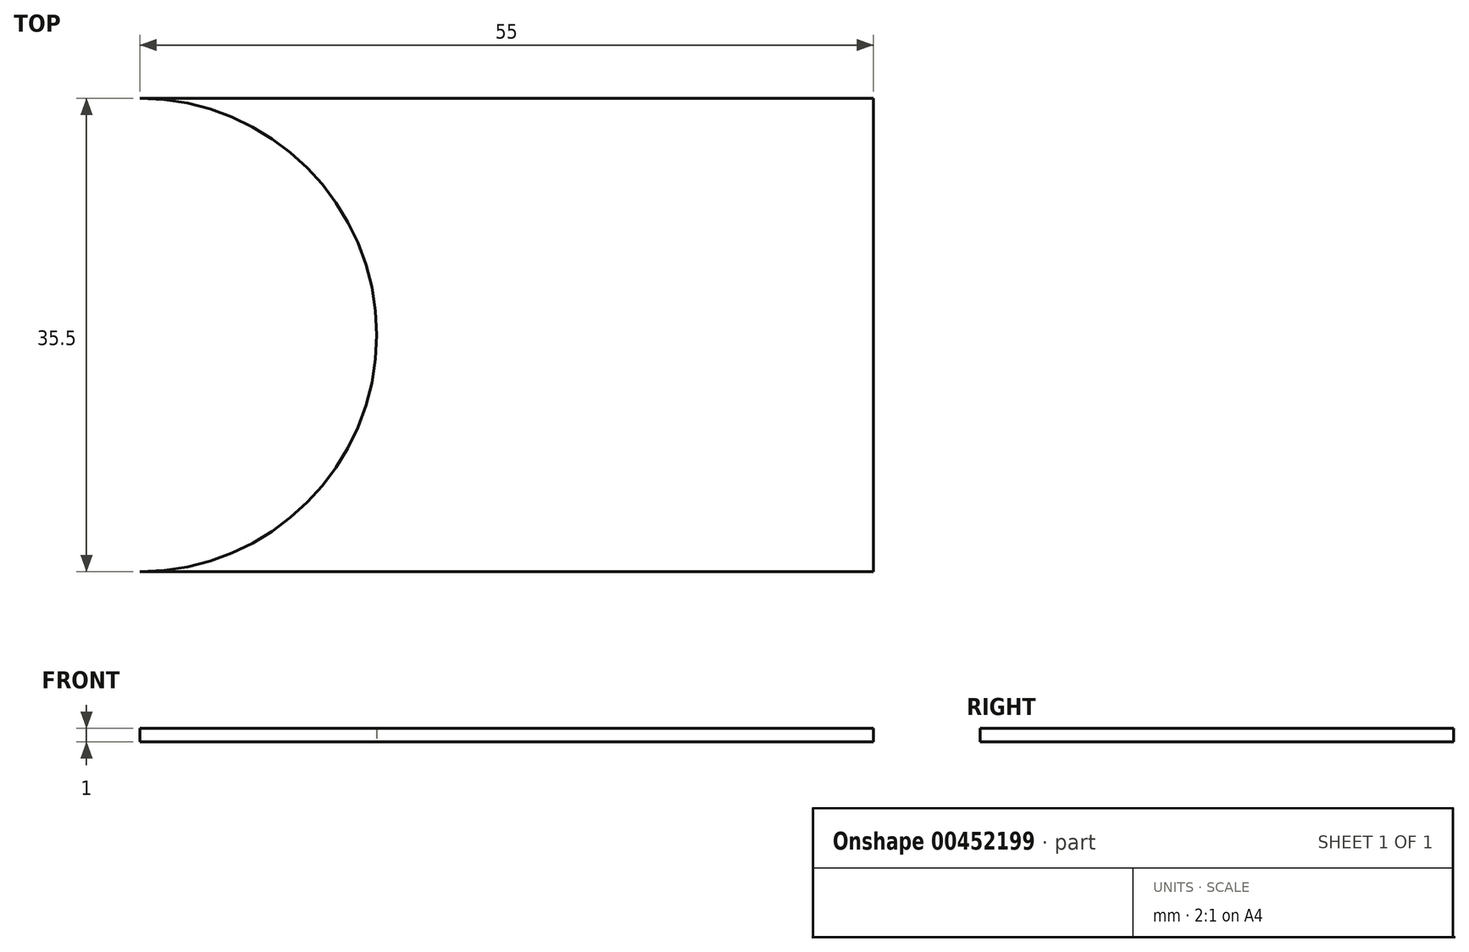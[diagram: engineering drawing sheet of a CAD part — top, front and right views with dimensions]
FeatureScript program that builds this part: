
annotation { "Feature Type Name" : "Feature", "Feature Type Description" : "" }
export const myFeature = defineFeature(function(context is Context, id is Id, definition is map)
    precondition{}
    {
        {
            var Q0;
            Q0=qCreatedBy(makeId("Top.planeOp"),FACE);
            var sketch = newSketch(context, id + "F0", { "sketchPlane" : qUnion([Q0])});
            skCircle(sketch, "E0", {"center": v(0, 0) * mm, "radius": 17.75 * mm});
            skLineSegment(sketch, "E1", {"start": v(0, -17.75) * mm, "end": v(55, -17.75) * mm});
            skLineSegment(sketch, "E2", {"start": v(0, 17.75) * mm, "end": v(55, 17.75) * mm});
            skLineSegment(sketch, "E3", {"start": v(55, 17.75) * mm, "end": v(55, -17.75) * mm});
            skSolve(sketch);
        }
        {
            var Q0;
            {var subQ0=sQuery(id+"F0.wireOp",EDGE,"E0");var subQ2=makeQuery(id+"F0.imprint","IMPRINT",VERTEX,{"derivedFrom":subQ0});Q0=makeQuery(id+"F0.imprint","IMPRINT",FACE,{"disambiguationData":[TD([[makeQuery(id+"F0.imprint","IMPRINT",EDGE,{"disambiguationData":[TD([[subQ2,-1.0]])],"derivedFrom":subQ0}),1.0]])]});}
            var Q1;
            {var subQ1=sQuery(id+"F0.wireOp",EDGE,"E1");Q1=makeQuery(id+"F0.imprint","IMPRINT",FACE,{"disambiguationData":[TD([[makeQuery(id+"F0.imprint","IMPRINT",EDGE,{"derivedFrom":subQ1}),1.0]])]});}
            extrude(context, id + "F1", {"entities" : qUnion([Q0, Q1]), "depth" : 1 * mm, "offsetDistance" : 25 * mm});
        }
    });
